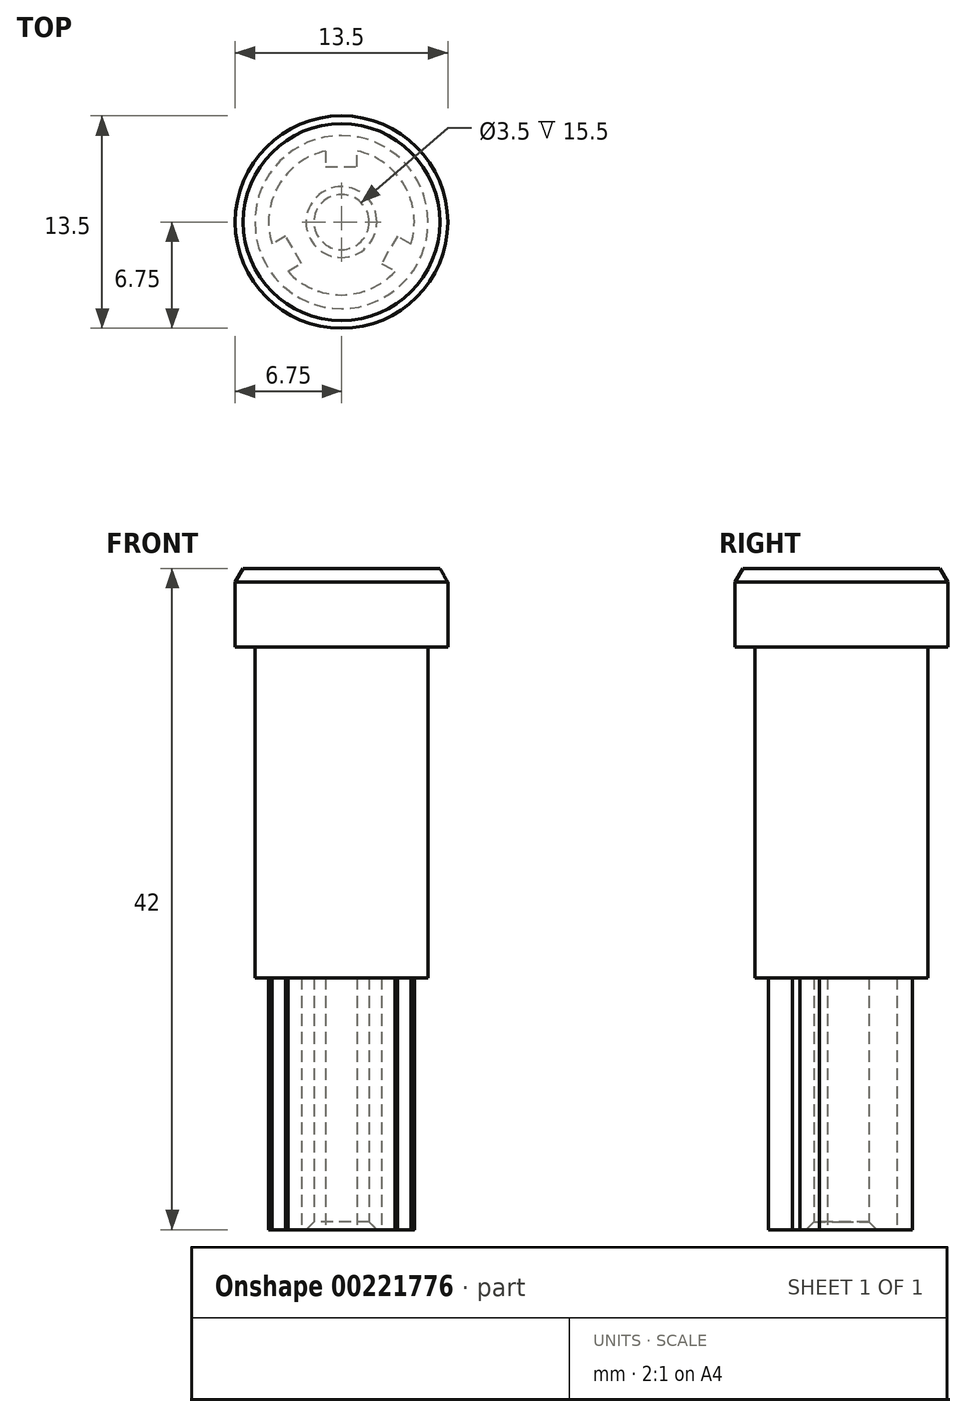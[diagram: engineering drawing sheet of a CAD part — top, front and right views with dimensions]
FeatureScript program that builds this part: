
annotation { "Feature Type Name" : "Feature", "Feature Type Description" : "" }
export const myFeature = defineFeature(function(context is Context, id is Id, definition is map)
    precondition{}
    {
        {
            var Q0;
            Q0=qCreatedBy(makeId("Top.planeOp"),FACE);
            var sketch = newSketch(context, id + "F0", { "sketchPlane" : qUnion([Q0])});
            skArc(sketch, "E0", {"start": v(-1, 4.52) * mm, "mid": v(-4, 2.31) * mm, "end": v(-4.41, -1.4) * mm});
            skLineSegment(sketch, "E1", {"start": v(-1, 4.52) * mm, "end": v(-1, 3.52) * mm});
            skLineSegment(sketch, "E2", {"start": v(-1, 3.52) * mm, "end": v(1, 3.52) * mm});
            skLineSegment(sketch, "E3", {"start": v(1, 3.52) * mm, "end": v(1, 4.52) * mm});
            skLineSegment(sketch, "E4.1.0", {"start": v(-3.54, -0.9) * mm, "end": v(-4.41, -1.4) * mm});
            skLineSegment(sketch, "E4.1.1", {"start": v(-2.54, -2.62) * mm, "end": v(-3.54, -0.9) * mm});
            skLineSegment(sketch, "E4.1.2", {"start": v(-3.41, -3.12) * mm, "end": v(-2.54, -2.62) * mm});
            skLineSegment(sketch, "E4.2.0", {"start": v(2.54, -2.62) * mm, "end": v(3.41, -3.12) * mm});
            skLineSegment(sketch, "E4.2.1", {"start": v(3.54, -0.9) * mm, "end": v(2.54, -2.62) * mm});
            skLineSegment(sketch, "E4.2.2", {"start": v(4.41, -1.4) * mm, "end": v(3.54, -0.9) * mm});
            skArc(sketch, "E5.trimOffspring", {"start": v(4.41, -1.4) * mm, "mid": v(4, 2.31) * mm, "end": v(1, 4.52) * mm});
            skArc(sketch, "E6.trimOffspring", {"start": v(-3.41, -3.12) * mm, "mid": v(0, -4.62) * mm, "end": v(3.41, -3.12) * mm});
            skCircle(sketch, "E7", {"center": v(0, 0) * mm, "radius": 1.75 * mm});
            skSolve(sketch);
        }
        {
            var Q0;
            Q0 = qSketchRegion(id + "F0", true);
            extrude(context, id + "F1", {"entities" : qUnion([Q0]), "depth" : 16 * mm});
        }
        {
            var Q0;
            Q0=makeQuery(id+"F1.opExtrude","CAP_FACE",FACE,{"disambiguationData":[OSD([sQuery(id+"F0.wireOp",EDGE,"E0"),sQuery(id+"F0.wireOp",EDGE,"E1"),sQuery(id+"F0.wireOp",EDGE,"E2"),sQuery(id+"F0.wireOp",EDGE,"E3"),sQuery(id+"F0.wireOp",EDGE,"E4.1.0"),sQuery(id+"F0.wireOp",EDGE,"E4.1.1"),sQuery(id+"F0.wireOp",EDGE,"E4.1.2"),sQuery(id+"F0.wireOp",EDGE,"E4.2.0"),sQuery(id+"F0.wireOp",EDGE,"E4.2.1"),sQuery(id+"F0.wireOp",EDGE,"E4.2.2"),sQuery(id+"F0.wireOp",EDGE,"E5.trimOffspring"),sQuery(id+"F0.wireOp",EDGE,"E6.trimOffspring"),sQuery(id+"F0.wireOp",EDGE,"E7")])],"isStart":false});
            var sketch = newSketch(context, id + "F2", { "sketchPlane" : qUnion([Q0])});
            skCircle(sketch, "E8", {"center": v(0, 0) * mm, "radius": 5.5 * mm});
            skSolve(sketch);
        }
        {
            var Q0;
            Q0 = qSketchRegion(id + "F2", true);
            extrude(context, id + "F3", {"entities" : qUnion([Q0]), "operationType" : NewBodyOperationType.ADD, "depth" : 21 * mm});
        }
        {
            var Q0;
            Q0=makeQuery(id+"F3.opExtrude","CAP_FACE",FACE,{"disambiguationData":[OSD([sQuery(id+"F2.wireOp",EDGE,"E8")])],"isStart":false});
            var sketch = newSketch(context, id + "F4", { "sketchPlane" : qUnion([Q0])});
            skCircle(sketch, "E9", {"center": v(0, 0) * mm, "radius": 6.75 * mm});
            skSolve(sketch);
        }
        {
            var Q0;
            Q0 = qSketchRegion(id + "F4", true);
            extrude(context, id + "F5", {"entities" : qUnion([Q0]), "operationType" : NewBodyOperationType.ADD, "depth" : 5 * mm});
        }
        {
            var Q0;
            Q0=makeQuery(id+"F5.opExtrude","CAP_FACE",FACE,{"disambiguationData":[OSD([sQuery(id+"F4.wireOp",EDGE,"E9")])],"isStart":false});
            chamfer(context, id + "F6", {"entities" : qUnion([Q0]), "chamferType" : ChamferType.OFFSET_ANGLE, "width" : .5 * mm, "oppositeDirection" : false, "angle" : 60 * degree, "tangentPropagation" : true});
        }
        {
            var Q0;
            Q0=makeQuery(id+"F1.opExtrude","CAP_EDGE",EDGE,{"disambiguationData":[OSD([sQuery(id+"F0.wireOp",EDGE,"E7")])],"isStart":true});
            chamfer(context, id + "F7", {"entities" : qUnion([Q0]), "width" : .5 * mm, "tangentPropagation" : true});
        }
    });
